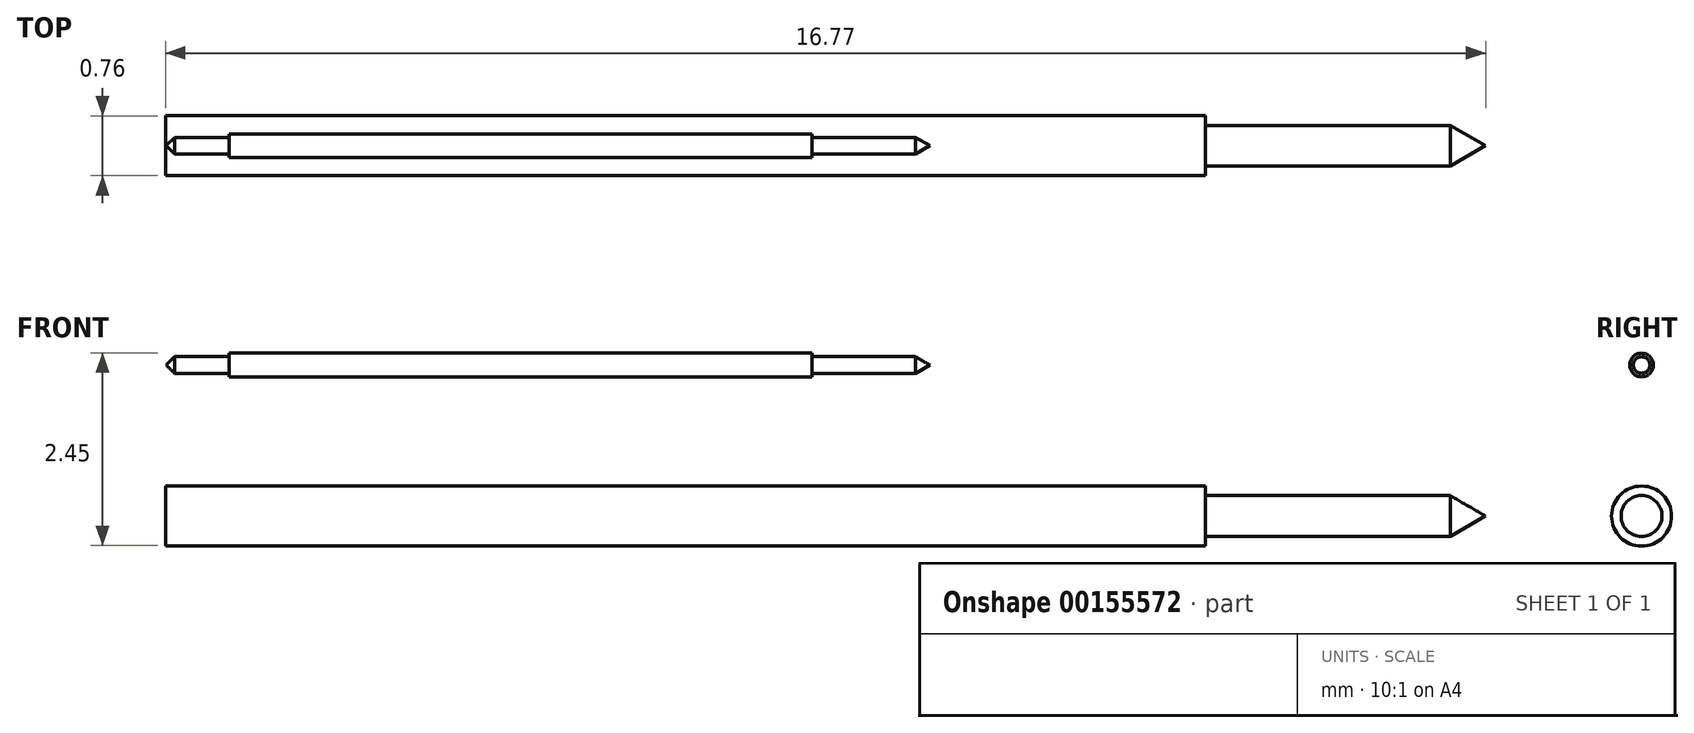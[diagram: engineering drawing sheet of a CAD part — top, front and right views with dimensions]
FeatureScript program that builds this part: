
annotation { "Feature Type Name" : "Feature", "Feature Type Description" : "" }
export const myFeature = defineFeature(function(context is Context, id is Id, definition is map)
    precondition{}
    {
        {
            var Q0;
            Q0=qCreatedBy(makeId("Front.planeOp"),FACE);
            var sketch = newSketch(context, id + "F0", { "sketchPlane" : qUnion([Q0])});
            skLineSegment(sketch, "E0.bottom", {"start": v(-37.5, 31.05) * mm, "end": v(-30.1, 31.05) * mm});
            skLineSegment(sketch, "E0.top", {"start": v(-37.5, 30.9) * mm, "end": v(-30.1, 30.9) * mm});
            skLineSegment(sketch, "E0.left", {"start": v(-37.5, 31.05) * mm, "end": v(-37.5, 30.9) * mm});
            skLineSegment(sketch, "E0.right", {"start": v(-30.1, 31.05) * mm, "end": v(-30.1, 30.9) * mm});
            skLineSegment(sketch, "E1.bottom", {"start": v(-30.1, 30.9) * mm, "end": v(-28.6, 30.9) * mm});
            skLineSegment(sketch, "E1.top", {"start": v(-30.1, 31) * mm, "end": v(-28.77, 31) * mm});
            skLineSegment(sketch, "E1.left", {"start": v(-30.1, 30.9) * mm, "end": v(-30.1, 31) * mm});
            skLineSegment(sketch, "E2.bottom", {"start": v(-37.5, 30.9) * mm, "end": v(-38.3, 30.9) * mm});
            skLineSegment(sketch, "E2.top", {"start": v(-37.5, 31) * mm, "end": v(-38.19, 31) * mm});
            skLineSegment(sketch, "E2.left", {"start": v(-37.5, 30.9) * mm, "end": v(-37.5, 31) * mm});
            skLineSegment(sketch, "E3", {"start": v(-38.3, 30.9) * mm, "end": v(-38.19, 31) * mm});
            skLineSegment(sketch, "E4", {"start": v(-28.6, 30.9) * mm, "end": v(-28.77, 31) * mm});
            skSolve(sketch);
        }
        {
            var Q0;
            Q0=makeQuery(id+"F0.imprint","IMPRINT",FACE,{"disambiguationData":[TD([[makeQuery(id+"F0.imprint","IMPRINT",EDGE,{"derivedFrom":sQuery(id+"F0.wireOp",EDGE,"E2.bottom")}),-1.0]])]});
            var Q1;
            Q1=makeQuery(id+"F0.imprint","IMPRINT",FACE,{"disambiguationData":[TD([[makeQuery(id+"F0.imprint","IMPRINT",EDGE,{"derivedFrom":sQuery(id+"F0.wireOp",EDGE,"E0.bottom")}),-1.0]])]});
            var Q2;
            Q2=makeQuery(id+"F0.imprint","IMPRINT",FACE,{"disambiguationData":[TD([[makeQuery(id+"F0.imprint","IMPRINT",EDGE,{"derivedFrom":sQuery(id+"F0.wireOp",EDGE,"E1.bottom")}),1.0]])]});
            var Q3;
            Q3=sQuery(id+"F0.wireOp",EDGE,"E0.top");
            revolve(context, id + "F1", {"entities" : qUnion([Q0, Q1, Q2]), "axis" : qUnion([Q3]), "revolveType" : RevolveType.FULL});
        }
        {
            var Q0;
            Q0=qCreatedBy(makeId("Front.planeOp"),FACE);
            var sketch = newSketch(context, id + "F2", { "sketchPlane" : qUnion([Q0])});
            skLineSegment(sketch, "E5.bottom", {"start": v(-38.3, 29.36) * mm, "end": v(-25.09, 29.36) * mm});
            skLineSegment(sketch, "E5.top", {"start": v(-38.3, 28.98) * mm, "end": v(-25.09, 28.98) * mm});
            skLineSegment(sketch, "E5.left", {"start": v(-38.3, 29.36) * mm, "end": v(-38.3, 28.98) * mm});
            skLineSegment(sketch, "E5.right", {"start": v(-25.09, 29.36) * mm, "end": v(-25.09, 28.98) * mm});
            skLineSegment(sketch, "E6.bottom", {"start": v(-25.09, 28.98) * mm, "end": v(-21.53, 28.98) * mm});
            skLineSegment(sketch, "E6.top", {"start": v(-25.09, 29.24) * mm, "end": v(-21.53, 29.24) * mm});
            skLineSegment(sketch, "E6.left", {"start": v(-25.09, 28.98) * mm, "end": v(-25.09, 29.24) * mm});
            skLineSegment(sketch, "E6.right", {"start": v(-21.53, 28.98) * mm, "end": v(-21.53, 29.24) * mm});
            skLineSegment(sketch, "E7", {"start": v(-21.53, 28.98) * mm, "end": v(-21.98, 29.24) * mm});
            skSolve(sketch);
        }
        {
            var Q0;
            Q0=makeQuery(id+"F2.imprint","IMPRINT",FACE,{"disambiguationData":[TD([[makeQuery(id+"F2.imprint","IMPRINT",EDGE,{"derivedFrom":sQuery(id+"F2.wireOp",EDGE,"E5.bottom")}),-1.0]])]});
            var Q1;
            Q1=makeQuery(id+"F2.imprint","IMPRINT",FACE,{"disambiguationData":[TD([[makeQuery(id+"F2.imprint","IMPRINT",EDGE,{"derivedFrom":sQuery(id+"F2.wireOp",EDGE,"E6.bottom")}),1.0]])]});
            var Q2;
            Q2=sQuery(id+"F2.wireOp",EDGE,"E5.top");
            revolve(context, id + "F3", {"entities" : qUnion([Q0, Q1]), "axis" : qUnion([Q2]), "revolveType" : RevolveType.FULL});
        }
    });
